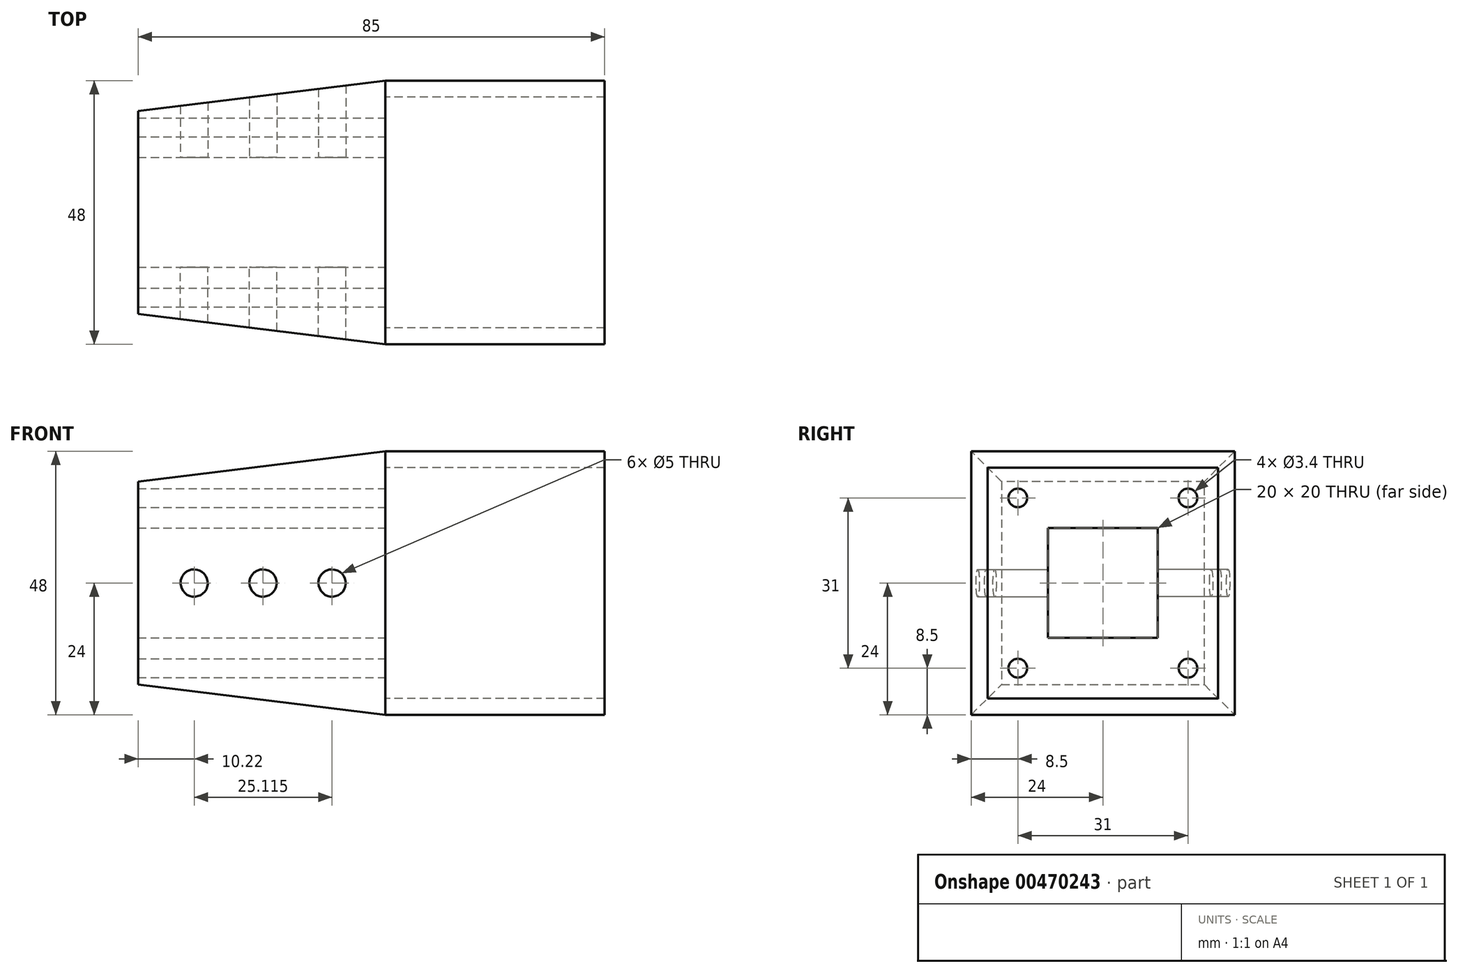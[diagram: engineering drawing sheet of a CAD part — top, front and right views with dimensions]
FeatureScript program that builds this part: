
annotation { "Feature Type Name" : "Feature", "Feature Type Description" : "" }
export const myFeature = defineFeature(function(context is Context, id is Id, definition is map)
    precondition{}
    {
        {
            var Q0;
            Q0=qCreatedBy(makeId("Right.planeOp"),FACE);
            var sketch = newSketch(context, id + "F0", { "sketchPlane" : qUnion([Q0])});
            skLineSegment(sketch, "E0.bottom", {"start": v(21, 21) * mm, "end": v(-21, 21) * mm});
            skLineSegment(sketch, "E0.top", {"start": v(21, -21) * mm, "end": v(-21, -21) * mm});
            skLineSegment(sketch, "E0.left", {"start": v(21, 21) * mm, "end": v(21, -21) * mm});
            skLineSegment(sketch, "E0.right", {"start": v(-21, 21) * mm, "end": v(-21, -21) * mm});
            skPoint(sketch, "E0.middle", {"position": v(0, 0) * mm});
            skLineSegment(sketch, "E1.bottom", {"start": v(10, 10) * mm, "end": v(-10, 10) * mm});
            skLineSegment(sketch, "E1.top", {"start": v(10, -10) * mm, "end": v(-10, -10) * mm});
            skLineSegment(sketch, "E1.left", {"start": v(10, 10) * mm, "end": v(10, -10) * mm});
            skLineSegment(sketch, "E1.right", {"start": v(-10, 10) * mm, "end": v(-10, -10) * mm});
            skLineSegment(sketch, "E2.bottom", {"start": v(15.5, 15.5) * mm, "end": v(-15.5, 15.5) * mm, "construction": true});
            skLineSegment(sketch, "E2.top", {"start": v(15.5, -15.5) * mm, "end": v(-15.5, -15.5) * mm, "construction": true});
            skLineSegment(sketch, "E2.left", {"start": v(15.5, 15.5) * mm, "end": v(15.5, -15.5) * mm, "construction": true});
            skLineSegment(sketch, "E2.right", {"start": v(-15.5, 15.5) * mm, "end": v(-15.5, -15.5) * mm, "construction": true});
            skLineSegment(sketch, "E3.0", {"start": v(24, 24) * mm, "end": v(-24, 24) * mm});
            skLineSegment(sketch, "E3.1", {"start": v(24, 24) * mm, "end": v(24, -24) * mm});
            skLineSegment(sketch, "E3.2", {"start": v(24, -24) * mm, "end": v(-24, -24) * mm});
            skLineSegment(sketch, "E3.3", {"start": v(-24, 24) * mm, "end": v(-24, -24) * mm});
            skSolve(sketch);
        }
        {
            var Q0;
            Q0=makeQuery(id+"F0.imprint","IMPRINT",FACE,{"disambiguationData":[TD([[makeQuery(id+"F0.imprint","IMPRINT",EDGE,{"derivedFrom":sQuery(id+"F0.wireOp",EDGE,"E0.bottom")}),-1.0]])]});
            var Q1;
            Q1=makeQuery(id+"F0.imprint","IMPRINT",FACE,{"disambiguationData":[TD([[makeQuery(id+"F0.imprint","IMPRINT",EDGE,{"derivedFrom":sQuery(id+"F0.wireOp",EDGE,"E0.bottom")}),1.0]])]});
            var Q2;
            Q2=makeQuery(id+"F0.imprint","IMPRINT",FACE,{"disambiguationData":[TD([[makeQuery(id+"F0.imprint","IMPRINT",EDGE,{"derivedFrom":sQuery(id+"F0.wireOp",EDGE,"E1.bottom")}),1.0]])]});
            extrude(context, id + "F1", {"entities" : qUnion([Q0, Q1, Q2]), "oppositeDirection" : true, "depth" : 45 * mm, "hasDraft" : true, "draftAngle" : 7 * degree, "draftPullDirection" : true});
        }
        {
            var Q0;
            Q0=makeQuery(id+"F0.imprint","IMPRINT",FACE,{"disambiguationData":[TD([[makeQuery(id+"F0.imprint","IMPRINT",EDGE,{"derivedFrom":sQuery(id+"F0.wireOp",EDGE,"E1.bottom")}),1.0]])]});
            extrude(context, id + "F2", {"entities" : qUnion([Q0]), "operationType" : NewBodyOperationType.REMOVE, "oppositeDirection" : true, "depth" : 60 * mm});
        }
        {
            var Q0;
            Q0=makeQuery(id+"F0.imprint","IMPRINT",FACE,{"disambiguationData":[TD([[makeQuery(id+"F0.imprint","IMPRINT",EDGE,{"derivedFrom":sQuery(id+"F0.wireOp",EDGE,"E0.bottom")}),-1.0]])]});
            extrude(context, id + "F3", {"entities" : qUnion([Q0]), "operationType" : NewBodyOperationType.ADD, "depth" : 40 * mm});
        }
        {
            var Q0;
            Q0=sQuery(id+"F0.wireOp",VERTEX,"E2.bottom.start");
            var Q1;
            Q1=sQuery(id+"F0.wireOp",VERTEX,"E2.right.start");
            var Q2;
            Q2=sQuery(id+"F0.wireOp",VERTEX,"E2.right.end");
            var Q3;
            Q3=sQuery(id+"F0.wireOp",VERTEX,"E2.top.start");
            var Q4;
            Q4=makeQuery(id+"F1.opExtrude","SWEPT_BODY",BODY,{"disambiguationData":[OSD([sQuery(id+"F0.wireOp",EDGE,"E3.0"),sQuery(id+"F0.wireOp",EDGE,"E3.1"),sQuery(id+"F0.wireOp",EDGE,"E3.2"),sQuery(id+"F0.wireOp",EDGE,"E3.3")])]});
            hole(context, id + "F4", {"style" : HoleStyle.SIMPLE, "endStyle" : HoleEndStyle.THROUGH, "holeDiameter" : 3.4 * mm, "isTappedThrough" : true, "tappedDepth" : 12 * mm, "tapClearance" : 3, "startFromSketch" : true, "locations" : qUnion([Q0, Q1, Q2, Q3]), "scope" : qUnion([Q4])});
        }
        {
            var Q0;
            Q0=makeQuery(id+"F2.boolean.opBoolean","COPY",FACE,{"derivedFrom":makeQuery(id+"F2.opExtrude","SWEPT_FACE",FACE,{"disambiguationData":[OSD([sQuery(id+"F0.wireOp",EDGE,"E1.right")])]})});
            var sketch = newSketch(context, id + "F5", { "sketchPlane" : qUnion([Q0])});
            skPoint(sketch, "E4", {"position": v(34.78, 0) * mm});
            skPoint(sketch, "E4.positionSnap0", {"position": v(45, 0) * mm});
            skPoint(sketch, "E5", {"position": v(22.24, 0) * mm});
            skPoint(sketch, "E6", {"position": v(9.66, 0) * mm});
            skSolve(sketch);
        }
        {
            var Q0;
            Q0=sQuery(id+"F5.wireOp",VERTEX,"E4");
            var Q1;
            Q1=sQuery(id+"F5.wireOp",VERTEX,"E5");
            var Q2;
            Q2=sQuery(id+"F5.wireOp",VERTEX,"E6");
            var Q3;
            Q3=makeQuery(id+"F1.opExtrude","SWEPT_BODY",BODY,{"disambiguationData":[OSD([sQuery(id+"F0.wireOp",EDGE,"E3.0"),sQuery(id+"F0.wireOp",EDGE,"E3.1"),sQuery(id+"F0.wireOp",EDGE,"E3.2"),sQuery(id+"F0.wireOp",EDGE,"E3.3")])]});
            hole(context, id + "F6", {"style" : HoleStyle.SIMPLE, "endStyle" : HoleEndStyle.BLIND, "holeDiameter" : 5 * mm, "holeDepth" : 69 * mm, "isTappedThrough" : true, "tappedDepth" : 12 * mm, "tapClearance" : 3, "startFromSketch" : true, "locations" : qUnion([Q0, Q1, Q2]), "scope" : qUnion([Q3])});
        }
        {
            var Q0;
            Q0=sQuery(id+"F5.wireOp",VERTEX,"E4");
            var Q1;
            Q1=sQuery(id+"F5.wireOp",VERTEX,"E5");
            var Q2;
            Q2=sQuery(id+"F5.wireOp",VERTEX,"E6");
            var Q3;
            Q3=makeQuery(id+"F1.opExtrude","SWEPT_BODY",BODY,{"disambiguationData":[OSD([sQuery(id+"F0.wireOp",EDGE,"E3.0"),sQuery(id+"F0.wireOp",EDGE,"E3.1"),sQuery(id+"F0.wireOp",EDGE,"E3.2"),sQuery(id+"F0.wireOp",EDGE,"E3.3")])]});
            hole(context, id + "F7", {"style" : HoleStyle.SIMPLE, "endStyle" : HoleEndStyle.BLIND, "oppositeDirection" : true, "holeDiameter" : 5 * mm, "holeDepth" : 69 * mm, "isTappedThrough" : true, "tappedDepth" : 12 * mm, "tapClearance" : 3, "startFromSketch" : true, "locations" : qUnion([Q0, Q1, Q2]), "scope" : qUnion([Q3])});
        }
    });
